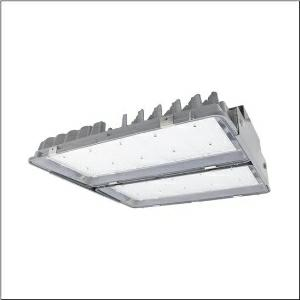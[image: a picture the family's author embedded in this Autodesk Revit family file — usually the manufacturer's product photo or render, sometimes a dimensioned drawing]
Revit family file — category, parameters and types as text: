
# Revit family: highbay_11xtreme_51hf81db4vma
name_source: partatom
category: Lighting Fixtures
units: mm (PartAtom-declared; Revit-internal decimal feet)

## family parameters
Cut with Voids When Loaded = No
Host = Face
Light Source = No
Part Type = Normal
Room Calculation Point = No
Round Connector Dimension = Use Diameter
Shared = No

## types (1)
- --- (1 x LED, 69400 lm, 380.2 W, 4000K)
    Apparent Load = 380 VA
    CIE Flux Codes = 88 96 99 100 100
    Color Rendering = 80
    Color Temperature = 4000K
    Default Elevation = 1800 mm
    Description = Highbay 11Xtreme, high bay luminaire, primary light control with lens, of PMMA, primary optical cover: cover, of toughened safety glass, light emission: direct distribution, primary light characteristic: symmetric, installation type: suspended mounting, surface-mounted, 2x LED module,for 1x 2x LED, rated luminous flux: 69.400lm, luminous efficacy: 183lm/W, light colour: 840, colour temperature: 4000K, control gear: DALI 2 (with two DALI addresses), with cable H07RN-F 5x 1.5mm², mains connection: 220..240V, AC, 50/60Hz, cable length: 1,5m, rated input power: 380W, luminaire housing, of diecast aluminium, partly coated, silver, length: 595mm, width: 560mm, height: 195mm, protection rating (complete): IP66, insulation class (complete): insulation class I (protective earthing), certification: CE, ENEC, UKCA, protection symbol: D, ball protection: ball impact resistant according to DIN VDE 0710 part 13 (with chain suspension), impact resistance: IK08, permissible operating ambient temperature: -25..+45°C, reducing of maximum allowable ambient temperature of 5°C with ceiling mounting, packaging unit: 1 piece
    Height = 157 mm
    Lamp = 1 x LED
    Lamp Light Flux = 69400 lm
    Lamp Power = 380.2 W
    Lamp count = 1
    Length = 593 mm
    Luminous efficacy = 183 lm/W
    Manufacturer = Siteco
    ModVariant = No
    Model = 51HF81DB4VMA
    Mounting Place = Ceiling
    Mounting Type = Pendant
    Number of Poles = 1
    OnlyDefault = Yes
    Power Factor = 1
    Product Name = Highbay 11Xtreme
    Product group = high bay luminaire
    ProductGroupID = 901
    Protection Class = Protection class I
    Protection Degree = IP 66
    RLX_Detail_Level = 1
    RLX_Emergency_Light_Flux = 0 lm
    RLX_Emergency_Type = 0
    RLX_Emergency_Type_DB = No
    RlxData = <blob elided: 33849 chars, md5=836e54a0>
    Socket = socket
    Standby Power = 0 W
    System Light Flux = 69402 lm
    System Power = 380 W
    Type Comments = factory setting: luminous flux: 100 % | dim-lin: 254 | 1257 mA
    Type Image = l_1258340.jpg
    URL = http://relux.com
    VarID = @adj_076744
    Voltage = 0 V
    Weight = 0.00 kg
    Width = 568 mm

## geometry (parser evidence)
native form markers: Blend x4, Sweep x9
no freeform markers — native parametric forms only
